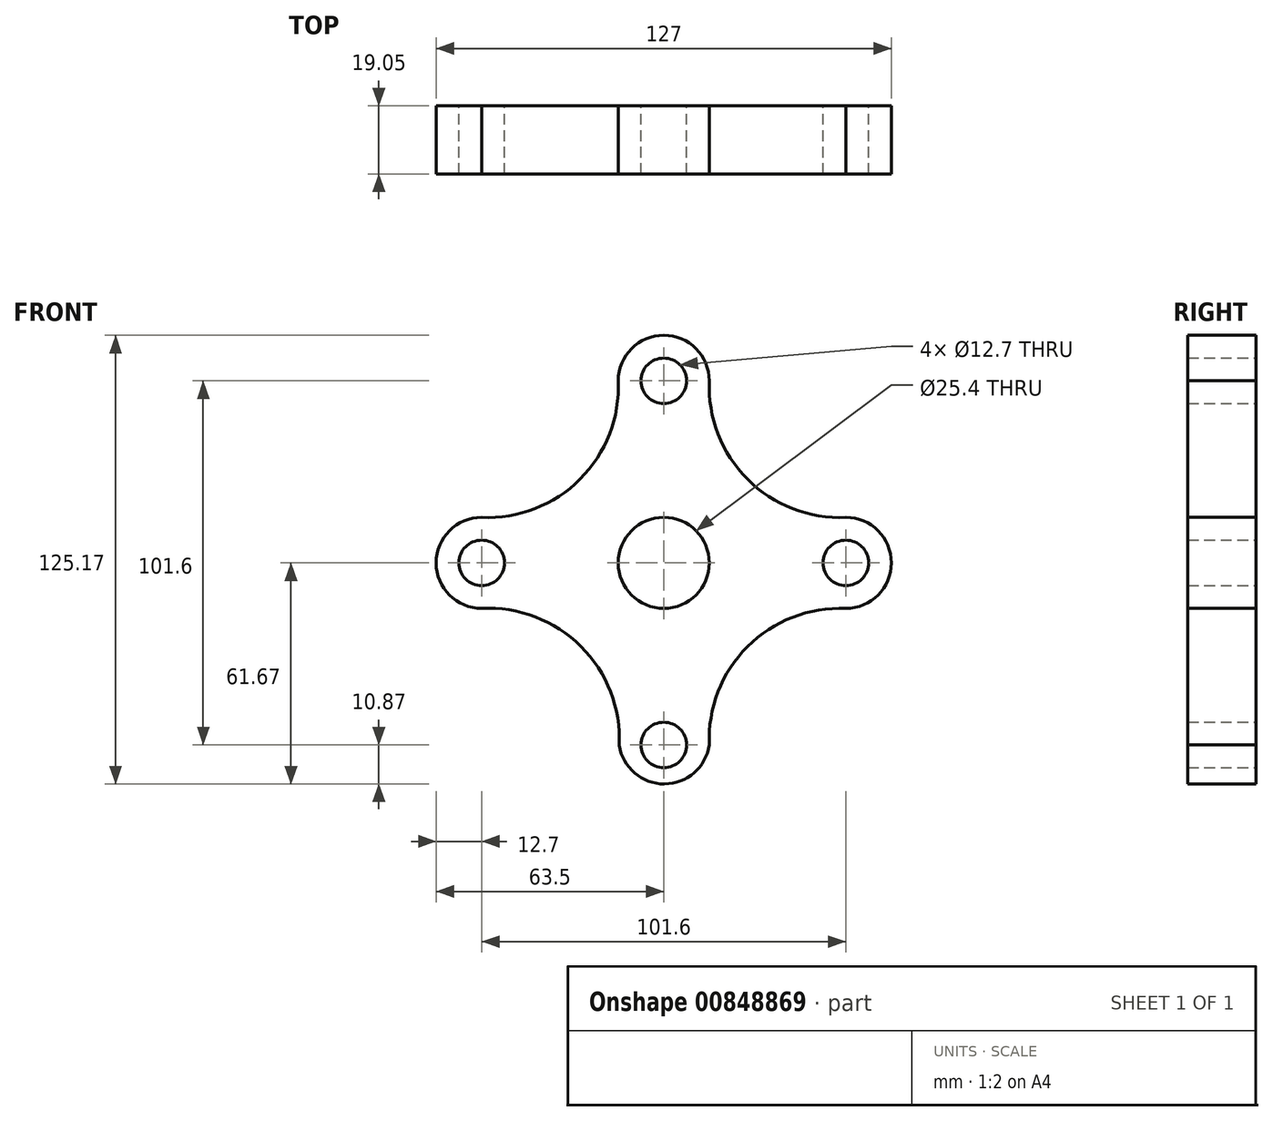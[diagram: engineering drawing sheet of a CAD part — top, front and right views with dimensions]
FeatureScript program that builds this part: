
annotation { "Feature Type Name" : "Feature", "Feature Type Description" : "" }
export const myFeature = defineFeature(function(context is Context, id is Id, definition is map)
    precondition{}
    {
        {
            var Q0;
            Q0=qCreatedBy(makeId("Front.planeOp"),FACE);
            var sketch = newSketch(context, id + "F0", { "sketchPlane" : qUnion([Q0])});
            skArc(sketch, "E0", {"start": v(-50.8, 12.7) * mm, "mid": v(-63.5, 0) * mm, "end": v(-50.8, -12.7) * mm});
            skArc(sketch, "E1", {"start": v(50.8, -12.7) * mm, "mid": v(63.5, 0) * mm, "end": v(50.8, 12.7) * mm});
            skArc(sketch, "E2", {"start": v(12.7, 50.8) * mm, "mid": v(0, 63.5) * mm, "end": v(-12.7, 50.8) * mm});
            skArc(sketch, "E3", {"start": v(-12.42, -50.9) * mm, "mid": v(0.18, -61.67) * mm, "end": v(12.7, -50.8) * mm});
            skArc(sketch, "E4", {"start": v(-12.42, -50.9) * mm, "mid": v(-23.14, -23.28) * mm, "end": v(-50.8, -12.7) * mm});
            skArc(sketch, "E5", {"start": v(50.8, -12.7) * mm, "mid": v(23.36, -23.36) * mm, "end": v(12.7, -50.8) * mm});
            skArc(sketch, "E6", {"start": v(-50.8, 12.7) * mm, "mid": v(-23.36, 23.36) * mm, "end": v(-12.7, 50.8) * mm});
            skArc(sketch, "E7", {"start": v(12.7, 50.8) * mm, "mid": v(23.36, 23.36) * mm, "end": v(50.8, 12.7) * mm});
            skSolve(sketch);
        }
        {
            var Q0;
            Q0 = qSketchRegion(id + "F0", true);
            extrude(context, id + "F1", {"entities" : qUnion([Q0]), "depth" : 19.05 * mm, "offsetDistance" : 25.4 * mm});
        }
        {
            var Q0;
            Q0=qCreatedBy(makeId("Front.planeOp"),FACE);
            var sketch = newSketch(context, id + "F2", { "sketchPlane" : qUnion([Q0])});
            skCircle(sketch, "E8", {"center": v(0, 50.8) * mm, "radius": 6.35 * mm});
            skCircle(sketch, "E9", {"center": v(50.8, 0) * mm, "radius": 6.35 * mm});
            skCircle(sketch, "E10", {"center": v(0, -50.8) * mm, "radius": 6.35 * mm});
            skCircle(sketch, "E11", {"center": v(-50.8, 0) * mm, "radius": 6.35 * mm});
            skCircle(sketch, "E12", {"center": v(0, 0) * mm, "radius": 12.7 * mm});
            skSolve(sketch);
        }
        {
            var Q0;
            Q0 = qSketchRegion(id + "F2", true);
            extrude(context, id + "F3", {"entities" : qUnion([Q0]), "operationType" : NewBodyOperationType.REMOVE, "depth" : 50.8 * mm, "offsetDistance" : 25.4 * mm});
        }
    });
